# Revit family: Drain-Linear_Pyramid_Noble_FreeStyle
name_source: partatom
category: Plumbing Fixtures
revit_build: Autodesk Revit 2014 (Build: 20130308_1515(x64)
units: mm (PartAtom-declared; Revit-internal decimal feet)

## types (14) — shared parameters
Assembly Code = D2030300
Building Codes = http://www.noblecompany.com
Default Elevation = 0"
GPM = 0 GPM
Installation-Fabrication = http://www.noblecompany.com
Manufacturer = Noble Company
Manufacturer Fax = 231-799-8850
Plate = Stainless Steel - Brushed
Product Data = http://www.noblecompany.com
Product Properties = http://www.noblecompany.com
URL = www.noblecompany.com
Weight = 10 lbs

## per-type parameters (varying)
| type | A | B | Base | C | D | Description | Model |
| 24in ABS | 24" | 21 3/4" | ABS | 15 3/4" | 1 1/4" | Freestyle 24 ABS - Pyramid Linear Drain | Freestyle 24 ABS - Pyramid |
| 32in ABS | 32" | 29 3/4" | ABS | 19 1/2" | 1 3/8" | Freestyle 32 ABS - Pyramid Linear Drain | Freestyle 32 ABS - Pyramid |
| 36in ABS | 36" | 33 3/4" | ABS | 21 3/4" | 1 3/8" | Freestyle 36 ABS - Pyramid Linear Drain | Freestyle 36 ABS - Pyramid |
| 40in ABS | 40" | 37 3/4" | ABS | 23 3/4" | 1 7/16" | Freestyle 40 ABS - Pyramid Linear Drain | Freestyle 40 ABS - Pyramid |
| 48in ABS | 48" | 45 3/4" | ABS | 27 3/4" | 1 1/2" | Freestyle 48 ABS - Pyramid Linear Drain | Freestyle 48 ABS - Pyramid |
| 54in ABS | 54" | 51 3/4" | ABS | 30 3/4" | 1 9/16" | Freestyle 54 ABS - Pyramid Linear Drain | Freestyle 54 ABS - Pyramid |
| 60in ABS | 60" | 57 3/4" | ABS | 33 3/4" | 1 5/8" | Freestyle 60 ABS - Pyramid Linear Drain | Freestyle 60 ABS - Pyramid |
| 24in PVC | 24" | 21 3/4" | PVC | 15 3/4" | 1 1/4" | Freestyle 24 PVC - Pyramid Linear Drain | Freestyle 24 PVC - Pyramid |
| 32in PVC | 32" | 29 3/4" | PVC | 19 1/2" | 1 3/8" | Freestyle 32 PVC - Pyramid Linear Drain | Freestyle 32 PVC - Pyramid |
| 36in PVC | 36" | 33 3/4" | PVC | 21 3/4" | 1 3/8" | Freestyle 36 PVC - Pyramid Linear Drain | Freestyle 36 PVC - Pyramid |
| 40in PVC | 40" | 37 3/4" | PVC | 23 3/4" | 1 7/16" | Freestyle 40 PVC - Pyramid Linear Drain | Freestyle 40 PVC - Pyramid |
| 48in PVC | 48" | 45 3/4" | PVC | 27 3/4" | 1 1/2" | Freestyle 48 PVC - Pyramid Linear Drain | Freestyle 48 PVC - Pyramid |
| 54in PVC | 54" | 51 3/4" | PVC | 30 3/4" | 1 9/16" | Freestyle 54 PVC - Pyramid Linear Drain | Freestyle 54 PVC - Pyramid |
| 60in PVC | 60" | 57 3/4" | PVC | 33 3/4" | 1 5/8" | Freestyle 60 PVC - Pyramid Linear Drain | Freestyle 60 PVC - Pyramid |

## geometry (parser evidence)
native form markers: Sweep x3
no freeform markers — native parametric forms only
